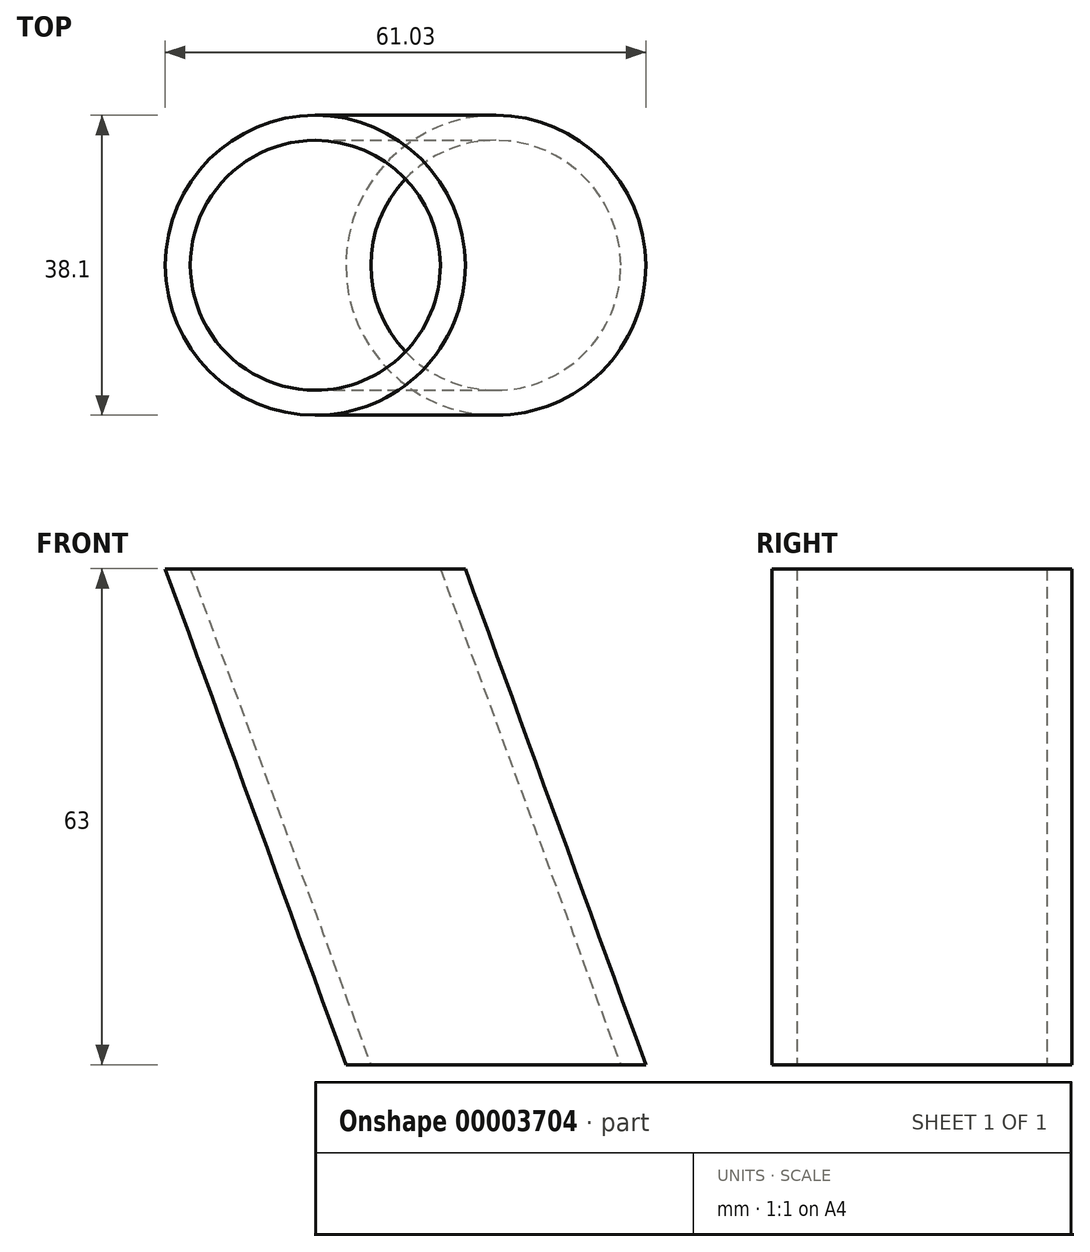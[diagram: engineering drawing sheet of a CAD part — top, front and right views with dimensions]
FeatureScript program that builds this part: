
annotation { "Feature Type Name" : "Feature", "Feature Type Description" : "" }
export const myFeature = defineFeature(function(context is Context, id is Id, definition is map)
    precondition{}
    {
        {
            var Q0;
            Q0=qCreatedBy(makeId("Top.planeOp"),FACE);
            var sketch = newSketch(context, id + "F0", { "sketchPlane" : qUnion([Q0])});
            skCircle(sketch, "E0", {"center": v(0, 0) * mm, "radius": 15.88 * mm});
            skCircle(sketch, "E1", {"center": v(0, 0) * mm, "radius": 19.05 * mm});
            skSolve(sketch);
        }
        {
            var Q0;
            Q0=qCreatedBy(makeId("Front.planeOp"),FACE);
            var sketch = newSketch(context, id + "F1", { "sketchPlane" : qUnion([Q0])});
            skLineSegment(sketch, "E2", {"start": v(0, 0) * mm, "end": v(0, 68.53) * mm, "construction": true});
            skLineSegment(sketch, "E3", {"start": v(0, 0) * mm, "end": v(-22.93, 63) * mm});
            skSolve(sketch);
        }
        {
            var Q0;
            Q0 = qSketchRegion(id + "F0", true);
            var Q1;
            Q1=sQuery(id+"F1.wireOp",EDGE,"E3");
            sweep(context, id + "F2", {"profiles" : qUnion([Q0]), "path" : qUnion([Q1])});
        }
    });
